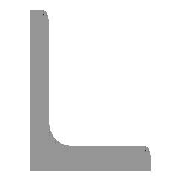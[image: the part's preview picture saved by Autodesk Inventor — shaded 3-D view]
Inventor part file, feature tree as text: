
AUTODESK INVENTOR PART (.ipt)
format: ipt  version: 2016 (Build 200138000, 138)  size: 129,536 bytes
history: native  units: mm (DEFAULTED — no unit token found)
features: other x4, sketch x3, extrude x2, plane x2
ambient origin geometry x8: Origin, YZ Plane, XZ Plane, XY Plane, X Axis, Y Axis, Z Axis, Center Point
bodies: Solid1 (feature_tree)
feature tree (11):
  parser-record x1  (decoder bookkeeping rows leaked as tree rows — omitted from the tree; the rows remain in map.json)
  other  "Driven Length"
  other  "Plano inicial"
  other  "Plano final"
  extrude  "Cuerpo"  Depth=38.1mm
  sketch  "Boceto5"  dims[d4=2400.0mm d5=0.0mm d10=0.0mm d11=0.0mm d12=-0.0mm d13=2400.0mm d14=4.826mm d15=2.286mm d16=90.0deg d17=2400.0mm d18=10.0mm d19=0.0mm]
  plane  "Plano de trabajo4"
  extrude  "Extrusión2"  Depth=4.7625mm
  sketch  "Sketch3"  dims[d0=38.1mm d1=38.1mm]
  plane  "Work Plane3"
  sketch  "Sketch4"  dims[d2=4.7625mm d3=4.7625mm]
